# Revit family: BE_84540_de_DE
name_source: partatom
category: Leuchten
units: mm (PartAtom-declared; Revit-internal decimal feet)

## family parameters
Basisbauteil = Fläche
Beim Laden mit Abzugskörper schneiden = Ja
Bemaßung runder Anschluss = Durchmesser verwenden
Gemeinsam genutzt = Nein
Lichtquelle = Nein
Raumberechnungspunkt = Ja
Teiletyp = Normal

## types (3) — shared parameters
AC/DC = AC/DC
Aktualisierung = 2022-05-19T04:00:07
BEGA_Dummy = Nein
BEGA_IES3 = Nein
BEGA_Intern = Ja
BEGA_Intern_Konstruktion = Ja
BEGA_Intern_an = Ja
BEGA_Intern_aus = Ja
Beschreibung = Hochleistungsscheinwerfer
Beschreibung_Sonderanfertigung = Hier können Sie Informationen zur Sonderanfertigung eintragen.
CE_Konformität = ja
ENEC = ja
Energieeffizienzklasse = LED A++ - A
Frequenz = 0/50-60 Hz
Gewicht = 21.95 kg
Hersteller = BEGA
Lampe = LED 300 W
Lastklassifizierung = Beleuchtung
Lebensdauerkriterien = L70B50 @ 25 °C = 100000 h
Logo = BEGA_Logo.png
M_A = Nein
M_G = Ja
M_W = Nein
Material_02 = BEGA_Oberfläche_Silber_matt
Material_03 = BEGA_Oberfläche_Weiss_matt
Material_04 = BEGA_Kunststoff_Grafit_matt
Material_06 = BEGA_Oberfläche_Edelstahl_gebürstet
Material_09 = BEGA_Glas_klar
Material_11 = BEGA_Glas_opal
Material_12 = BEGA_Kunststoff_klar
Material_15 = BEGA_Leuchtmedium_matt
Material_17 = BEGA_Reflektor
Material_18 = BEGA_Gummi_schwarz
Produktdatenblatt = https://cdn.bega.com
Scheinlast = 0 VA
Schutzart = IP 67
Schutzklasse = I
Sonderanfertigung = Nein
Spannung = 240 V
Typenbild = 84540.png
URL = https://www.bega.com
Umgebungstemperatur = 25 °C
Windangriffsfläche = 0.2 m²
zero-valued in all types: Vorgabe-Ansicht

## per-type parameters (varying)
| type | BEGA_IES1 | BEGA_IES2 | Bestellnummer | Farbtemperatur | Farbwiedergabeindex | LED_Modulbezeichnung | Lampenlichtstrom | Leuchtenlichtstrom | Modell |
| BEGA_84540_Grafit_K4 | Nein | Ja | 84540K4 | 4000 K | CRI > 80 | 3x LED-0699/840 + LED-0698/840 | 48120 lm | 15163 lm | 84540K4 |
| BEGA_84540_Grafit_K3 | Ja | Nein | 84540K3 | 3000 K | CRI > 80 | 3x LED-0699/830 + LED-0698/830 | 46920 lm | 14785 lm | 84540K3 |
| BEGA_84540_Grafit_K22 | Nein | Ja | 84540K22 | 2200 K | CRI > 65 | 3x LED-0699/622 + LED-0698/622 | 44580 lm | 14047 lm | 84540K22 |

## geometry (parser evidence)
native form markers: Blend x2, Sweep x15
no freeform markers — native parametric forms only
